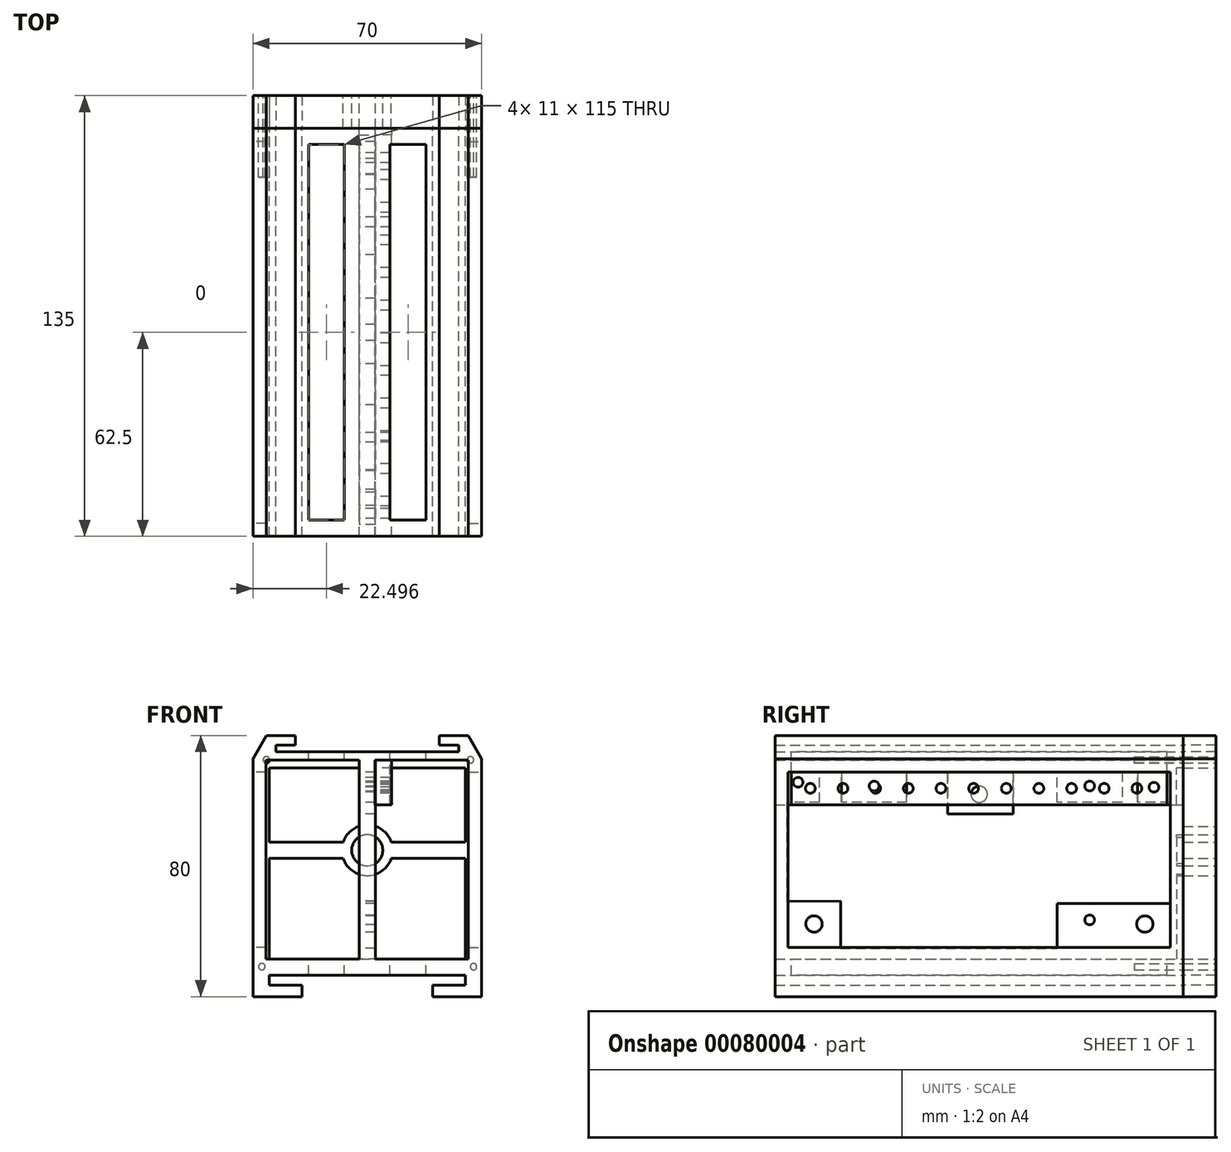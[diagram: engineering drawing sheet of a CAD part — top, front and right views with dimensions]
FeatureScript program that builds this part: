
annotation { "Feature Type Name" : "Feature", "Feature Type Description" : "" }
export const myFeature = defineFeature(function(context is Context, id is Id, definition is map)
    precondition{}
    {
        {
            var Q0;
            Q0=qCreatedBy(makeId("Front.planeOp"),FACE);
            var sketch = newSketch(context, id + "F0", { "sketchPlane" : qUnion([Q0])});
            skLineSegment(sketch, "E0", {"start": v(-44.21, 35.4) * mm, "end": v(-53.11, 35.4) * mm});
            skLineSegment(sketch, "E1", {"start": v(-57.21, 25.4) * mm, "end": v(-57.21, -44.6) * mm});
            skLineSegment(sketch, "E2", {"start": v(-57.21, -44.6) * mm, "end": v(-42.21, -44.6) * mm});
            skLineSegment(sketch, "E3", {"start": v(-42.21, -44.6) * mm, "end": v(-42.21, -41.16) * mm});
            skLineSegment(sketch, "E4", {"start": v(-42.21, -41.16) * mm, "end": v(-52.21, -41.16) * mm});
            skLineSegment(sketch, "E5", {"start": v(-52.21, -41.16) * mm, "end": v(-52.21, -38.06) * mm});
            skLineSegment(sketch, "E6", {"start": v(-52.21, -38.06) * mm, "end": v(-22.21, -38.06) * mm});
            skLineSegment(sketch, "E7", {"start": v(-44.21, 35.4) * mm, "end": v(-44.21, 32.4) * mm});
            skLineSegment(sketch, "E8", {"start": v(-44.21, 32.4) * mm, "end": v(-50.21, 32.4) * mm});
            skLineSegment(sketch, "E9", {"start": v(-50.21, 32.4) * mm, "end": v(-50.21, 30.4) * mm});
            skLineSegment(sketch, "E10", {"start": v(-50.21, 30.4) * mm, "end": v(-22.21, 30.4) * mm});
            skLineSegment(sketch, "E11", {"start": v(-22.21, 30.4) * mm, "end": v(-22.21, -38.06) * mm, "construction": true});
            skLineSegment(sketch, "E12.MirrorCS", {"start": v(-0.21, 35.4) * mm, "end": v(-0.21, 32.4) * mm});
            skLineSegment(sketch, "E13.MirrorCS", {"start": v(7.79, -41.16) * mm, "end": v(7.79, -38.06) * mm});
            skLineSegment(sketch, "E14.MirrorCS", {"start": v(-0.21, 32.4) * mm, "end": v(5.79, 32.4) * mm});
            skLineSegment(sketch, "E15.MirrorCS", {"start": v(-2.21, -41.16) * mm, "end": v(7.79, -41.16) * mm});
            skLineSegment(sketch, "E16.MirrorCS", {"start": v(-2.21, -44.6) * mm, "end": v(-2.21, -41.16) * mm});
            skLineSegment(sketch, "E17.MirrorCS", {"start": v(5.79, 32.4) * mm, "end": v(5.79, 30.4) * mm});
            skLineSegment(sketch, "E18.MirrorCS", {"start": v(5.79, 30.4) * mm, "end": v(-22.21, 30.4) * mm});
            skLineSegment(sketch, "E19.MirrorCS", {"start": v(12.79, 25.4) * mm, "end": v(12.79, -44.6) * mm});
            skLineSegment(sketch, "E20.MirrorCS", {"start": v(12.79, -44.6) * mm, "end": v(-2.21, -44.6) * mm});
            skLineSegment(sketch, "E21.MirrorCS", {"start": v(7.79, -38.06) * mm, "end": v(-22.21, -38.06) * mm});
            skLineSegment(sketch, "E22", {"start": v(-57.21, 25.4) * mm, "end": v(-57.21, 28.2) * mm});
            skPoint(sketch, "E23.start.orphan", {"position": v(-70.21, 35.4) * mm});
            skPoint(sketch, "E24.start.orphan", {"position": v(-62.21, 19.4) * mm});
            skPoint(sketch, "E25.start.orphan", {"position": v(-59.21, 19.4) * mm});
            skPoint(sketch, "E26.start.orphan", {"position": v(-59.21, 25.4) * mm});
            skPoint(sketch, "E27.MirrorCS.start.orphan", {"position": v(14.79, 25.4) * mm});
            skPoint(sketch, "E28.MirrorCS.end.orphan", {"position": v(14.79, 19.4) * mm});
            skPoint(sketch, "E28.MirrorCS.start.orphan", {"position": v(17.79, 19.4) * mm});
            skPoint(sketch, "E29.MirrorCS.end.orphan", {"position": v(25.79, 35.4) * mm});
            skLineSegment(sketch, "E30.MirrorCS", {"start": v(-92.21, 30.4) * mm, "end": v(-92.21, -38.06) * mm, "construction": true});
            skLineSegment(sketch, "E31.MirrorCS", {"start": v(-0.21, 35.4) * mm, "end": v(8.68, 35.4) * mm});
            skLineSegment(sketch, "E32.MirrorCS", {"start": v(12.79, 25.4) * mm, "end": v(12.79, 28.2) * mm});
            skPoint(sketch, "E33.MirrorCS.end.orphan", {"position": v(-57.21, 35.4) * mm});
            skLineSegment(sketch, "E34", {"start": v(-53.11, 35.4) * mm, "end": v(-57.21, 28.2) * mm});
            skLineSegment(sketch, "E35.MirrorCS", {"start": v(-73.15, 59.43) * mm, "end": v(-132.06, 24.57) * mm, "construction": true});
            skLineSegment(sketch, "E36.MirrorCS", {"start": v(8.68, 35.4) * mm, "end": v(12.79, 28.2) * mm});
            skPoint(sketch, "E37.MirrorCS.end.orphan", {"position": v(-53.11, 35.4) * mm});
            skPoint(sketch, "E37.MirrorCS.start.orphan", {"position": v(-57.64, 43.05) * mm});
            skPoint(sketch, "E38.orphan", {"position": v(12.79, 35.4) * mm});
            skSolve(sketch);
        }
        {
            var Q0;
            Q0 = qSketchRegion(id + "F0", true);
            extrude(context, id + "F1", {"entities" : qUnion([Q0]), "depth" : 125 * mm});
        }
        {
            var Q0;
            Q0=makeQuery(id+"F1.opExtrude","CAP_FACE",FACE,{"disambiguationData":[OSD([sQuery(id+"F0.wireOp",EDGE,"E0"),sQuery(id+"F0.wireOp",EDGE,"E1"),sQuery(id+"F0.wireOp",EDGE,"E2"),sQuery(id+"F0.wireOp",EDGE,"E3"),sQuery(id+"F0.wireOp",EDGE,"E4"),sQuery(id+"F0.wireOp",EDGE,"E5"),sQuery(id+"F0.wireOp",EDGE,"E6"),sQuery(id+"F0.wireOp",EDGE,"E7"),sQuery(id+"F0.wireOp",EDGE,"E8"),sQuery(id+"F0.wireOp",EDGE,"E9"),sQuery(id+"F0.wireOp",EDGE,"E10"),sQuery(id+"F0.wireOp",EDGE,"E12.MirrorCS"),sQuery(id+"F0.wireOp",EDGE,"E13.MirrorCS"),sQuery(id+"F0.wireOp",EDGE,"E14.MirrorCS"),sQuery(id+"F0.wireOp",EDGE,"E15.MirrorCS"),sQuery(id+"F0.wireOp",EDGE,"E16.MirrorCS"),sQuery(id+"F0.wireOp",EDGE,"E17.MirrorCS"),sQuery(id+"F0.wireOp",EDGE,"E18.MirrorCS"),sQuery(id+"F0.wireOp",EDGE,"E19.MirrorCS"),sQuery(id+"F0.wireOp",EDGE,"E20.MirrorCS"),sQuery(id+"F0.wireOp",EDGE,"E21.MirrorCS"),sQuery(id+"F0.wireOp",EDGE,"E22"),sQuery(id+"F0.wireOp",EDGE,"E31.MirrorCS"),sQuery(id+"F0.wireOp",EDGE,"E32.MirrorCS"),sQuery(id+"F0.wireOp",EDGE,"E34"),sQuery(id+"F0.wireOp",EDGE,"E36.MirrorCS")])],"isStart":true});
            var sketch = newSketch(context, id + "F2", { "sketchPlane" : qUnion([Q0])});
            skLineSegment(sketch, "E39", {"start": v(-8.79, 27.9) * mm, "end": v(-8.79, -33.06) * mm});
            skLineSegment(sketch, "E40", {"start": v(-8.79, -33.06) * mm, "end": v(19.71, -33.06) * mm});
            skLineSegment(sketch, "E41", {"start": v(19.71, -33.06) * mm, "end": v(19.71, 27.9) * mm});
            skLineSegment(sketch, "E42", {"start": v(19.71, 27.9) * mm, "end": v(-8.79, 27.9) * mm});
            skPoint(sketch, "E43", {"position": v(22.21, 30.4) * mm});
            skPoint(sketch, "E44", {"position": v(22.21, -38.06) * mm});
            skLineSegment(sketch, "E45", {"start": v(22.21, 30.4) * mm, "end": v(22.21, -38.06) * mm, "construction": true});
            skLineSegment(sketch, "E46.MirrorCS", {"start": v(53.21, 27.9) * mm, "end": v(53.21, -33.06) * mm});
            skLineSegment(sketch, "E47.MirrorCS", {"start": v(24.71, 27.9) * mm, "end": v(53.21, 27.9) * mm});
            skLineSegment(sketch, "E48.MirrorCS", {"start": v(24.71, -33.06) * mm, "end": v(24.71, 27.9) * mm});
            skLineSegment(sketch, "E49.MirrorCS", {"start": v(53.21, -33.06) * mm, "end": v(24.71, -33.06) * mm});
            skSolve(sketch);
        }
        {
            var Q0;
            Q0 = qSketchRegion(id + "F2", true);
            extrude(context, id + "F3", {"entities" : qUnion([Q0]), "operationType" : NewBodyOperationType.REMOVE, "oppositeDirection" : true, "depth" : 152.27 * mm});
        }
        {
            var Q0;
            Q0=makeQuery(id+"F1.opExtrude","SWEPT_FACE",FACE,{"disambiguationData":[OSD([sQuery(id+"F0.wireOp",EDGE,"E1"),sQuery(id+"F0.wireOp",EDGE,"E22")])]});
            var sketch = newSketch(context, id + "F4", { "sketchPlane" : qUnion([Q0])});
            skLineSegment(sketch, "E50", {"start": v(4, 24.2) * mm, "end": v(4, -29.6) * mm});
            skLineSegment(sketch, "E51", {"start": v(4, -29.6) * mm, "end": v(121, -29.6) * mm});
            skLineSegment(sketch, "E52", {"start": v(121, -29.6) * mm, "end": v(121, 24.2) * mm});
            skLineSegment(sketch, "E53", {"start": v(121, 24.2) * mm, "end": v(4, 24.2) * mm});
            skSolve(sketch);
        }
        {
            var Q0;
            Q0 = qSketchRegion(id + "F4", true);
            extrude(context, id + "F5", {"entities" : qUnion([Q0]), "operationType" : NewBodyOperationType.REMOVE, "oppositeDirection" : true, "depth" : 25 * mm});
        }
        {
            var Q0;
            Q0=makeQuery(id+"F3.boolean.opBoolean","COPY",FACE,{"derivedFrom":makeQuery(id+"F3.opExtrude","SWEPT_FACE",FACE,{"disambiguationData":[OSD([sQuery(id+"F2.wireOp",EDGE,"E41")])]})});
            var Q1;
            Q1=makeQuery(id+"F3.boolean.opBoolean","COPY",FACE,{"derivedFrom":makeQuery(id+"F3.opExtrude","SWEPT_FACE",FACE,{"disambiguationData":[OSD([sQuery(id+"F2.wireOp",EDGE,"E48.MirrorCS")])]})});
            cPlane(context, id + "F6", {"entities" : qUnion([Q0, Q1]), "cplaneType" : CPlaneType.MID_PLANE, "offset" : 150 * mm, "width" : 150 * mm, "height" : 150 * mm});
        }
        {
            var Q0;
            Q0=makeQuery(id+"F5.boolean.opBoolean","COPY",FACE,{"derivedFrom":makeQuery(id+"F5.opExtrude","SWEPT_FACE",FACE,{"disambiguationData":[OSD([sQuery(id+"F4.wireOp",EDGE,"E50")])]})});
            var Q1;
            Q1=makeQuery(id+"F5.boolean.opBoolean","COPY",FACE,{"derivedFrom":makeQuery(id+"F5.opExtrude","SWEPT_FACE",FACE,{"disambiguationData":[OSD([sQuery(id+"F4.wireOp",EDGE,"E51")])]})});
            var Q2;
            Q2=makeQuery(id+"F5.boolean.opBoolean","COPY",FACE,{"derivedFrom":makeQuery(id+"F5.opExtrude","SWEPT_FACE",FACE,{"disambiguationData":[OSD([sQuery(id+"F4.wireOp",EDGE,"E52")])]})});
            var Q3;
            Q3=makeQuery(id+"F5.boolean.opBoolean","COPY",FACE,{"derivedFrom":makeQuery(id+"F5.opExtrude","SWEPT_FACE",FACE,{"disambiguationData":[OSD([sQuery(id+"F4.wireOp",EDGE,"E53")])]})});
            var Q4;
            Q4=qCreatedBy(id+"F6.planeOp",FACE);
            mirror(context, id + "F7", {"operationType" : NewBodyOperationType.REMOVE, "faces" : qUnion([Q0, Q1, Q2, Q3]), "mirrorPlane" : qUnion([Q4]), "patternType" : MirrorType.FACE});
        }
        {
            var Q0;
            Q0=makeQuery(id+"F3.boolean.opBoolean","COPY",FACE,{"derivedFrom":makeQuery(id+"F3.opExtrude","SWEPT_FACE",FACE,{"disambiguationData":[OSD([sQuery(id+"F2.wireOp",EDGE,"E48.MirrorCS")])]})});
            var sketch = newSketch(context, id + "F8", { "sketchPlane" : qUnion([Q0])});
            skCircle(sketch, "E54", {"center": v(28.68, 19.9) * mm, "radius": 1.5 * mm});
            skCircle(sketch, "E55", {"center": v(94.68, 19.9) * mm, "radius": 1.5 * mm});
            skCircle(sketch, "E56", {"center": v(28.68, -21.1) * mm, "radius": 1.5 * mm});
            skLineSegment(sketch, "E57", {"start": v(18.68, 24.2) * mm, "end": v(18.68, 14.9) * mm});
            skLineSegment(sketch, "E58", {"start": v(18.68, 14.9) * mm, "end": v(38.68, 14.9) * mm});
            skLineSegment(sketch, "E59", {"start": v(38.68, 14.9) * mm, "end": v(38.68, 24.16) * mm});
            skLineSegment(sketch, "E60", {"start": v(38.68, 24.16) * mm, "end": v(84.68, 24.16) * mm});
            skLineSegment(sketch, "E61", {"start": v(84.68, 24.16) * mm, "end": v(84.68, 14.9) * mm});
            skLineSegment(sketch, "E62", {"start": v(84.68, 14.9) * mm, "end": v(104.68, 14.9) * mm});
            skLineSegment(sketch, "E63", {"start": v(104.68, 14.9) * mm, "end": v(104.68, 24.2) * mm});
            skLineSegment(sketch, "E64", {"start": v(104.68, 24.2) * mm, "end": v(121.44, 24.2) * mm});
            skLineSegment(sketch, "E65", {"start": v(121.44, 24.2) * mm, "end": v(121.44, -29.8) * mm});
            skLineSegment(sketch, "E66", {"start": v(121.44, -29.8) * mm, "end": v(38.68, -29.8) * mm});
            skLineSegment(sketch, "E67", {"start": v(38.68, -29.8) * mm, "end": v(38.68, -16.1) * mm});
            skLineSegment(sketch, "E68", {"start": v(38.68, -16.1) * mm, "end": v(18.68, -16.1) * mm});
            skLineSegment(sketch, "E69", {"start": v(18.68, -16.1) * mm, "end": v(18.68, -29.6) * mm});
            skLineSegment(sketch, "E70", {"start": v(18.68, -29.6) * mm, "end": v(4, -29.6) * mm});
            skLineSegment(sketch, "E71", {"start": v(4, -29.6) * mm, "end": v(4, 24.2) * mm});
            skLineSegment(sketch, "E72", {"start": v(4, 24.2) * mm, "end": v(18.68, 24.2) * mm});
            skLineSegment(sketch, "E73", {"start": v(4, 14.9) * mm, "end": v(14, 14.9) * mm});
            skLineSegment(sketch, "E74", {"start": v(14, 14.9) * mm, "end": v(14, 24.2) * mm});
            skLineSegment(sketch, "E75", {"start": v(111.44, 14.9) * mm, "end": v(121.44, 14.9) * mm});
            skLineSegment(sketch, "E76", {"start": v(111.44, 14.9) * mm, "end": v(111.44, 24.2) * mm});
            skPoint(sketch, "E77", {"position": v(9, 14.9) * mm});
            skPoint(sketch, "E78", {"position": v(14, 19.54) * mm});
            skCircle(sketch, "E79", {"center": v(9, 19.54) * mm, "radius": 1.5 * mm});
            skPoint(sketch, "E80", {"position": v(111.44, 19.54) * mm});
            skPoint(sketch, "E81", {"position": v(116.44, 14.9) * mm});
            skCircle(sketch, "E82", {"center": v(117.98, 21.07) * mm, "radius": 1.5 * mm});
            skCircle(sketch, "E83", {"center": v(113.09, -22.34) * mm, "radius": 2.5 * mm});
            skCircle(sketch, "E84", {"center": v(11.76, -22.4) * mm, "radius": 2.5 * mm});
            skCircle(sketch, "E85", {"center": v(62.5, 17.4) * mm, "radius": 2.5 * mm});
            skPoint(sketch, "E85.centerSnap0", {"position": v(62.5, 27.9) * mm});
            skLineSegment(sketch, "E86", {"start": v(104.9, -29.8) * mm, "end": v(104.9, -15.36) * mm});
            skLineSegment(sketch, "E87", {"start": v(104.9, -15.36) * mm, "end": v(121.44, -15.4) * mm});
            skLineSegment(sketch, "E88", {"start": v(18.68, -16.1) * mm, "end": v(4, -16.1) * mm});
            skLineSegment(sketch, "E89", {"start": v(52.1, 24.16) * mm, "end": v(52.1, 11.4) * mm});
            skLineSegment(sketch, "E90", {"start": v(52.1, 11.4) * mm, "end": v(72.17, 11.4) * mm});
            skLineSegment(sketch, "E91", {"start": v(72.17, 11.4) * mm, "end": v(72.17, 24.16) * mm});
            skSolve(sketch);
        }
        {
            var Q0;
            {var subQ7=sQuery(id+"F8.wireOp",EDGE,"E57");Q0=makeQuery(id+"F8.imprint","IMPRINT",FACE,{"disambiguationData":[TD([[makeQuery(id+"F8.imprint","IMPRINT",EDGE,{"derivedFrom":subQ7}),-1.0]])]});}
            var Q1;
            Q1=makeQuery(id+"F8.imprint","IMPRINT",FACE,{"disambiguationData":[TD([[makeQuery(id+"F8.imprint","IMPRINT",EDGE,{"derivedFrom":sQuery(id+"F8.wireOp",EDGE,"E79")}),1.0]])]});
            var Q2;
            Q2=makeQuery(id+"F8.imprint","IMPRINT",FACE,{"disambiguationData":[TD([[makeQuery(id+"F8.imprint","IMPRINT",EDGE,{"derivedFrom":sQuery(id+"F8.wireOp",EDGE,"E54")}),1.0]])]});
            var Q3;
            Q3=makeQuery(id+"F8.imprint","IMPRINT",FACE,{"disambiguationData":[TD([[makeQuery(id+"F8.imprint","IMPRINT",EDGE,{"derivedFrom":sQuery(id+"F8.wireOp",EDGE,"E55")}),1.0]])]});
            var Q4;
            Q4=makeQuery(id+"F8.imprint","IMPRINT",FACE,{"disambiguationData":[TD([[makeQuery(id+"F8.imprint","IMPRINT",EDGE,{"derivedFrom":sQuery(id+"F8.wireOp",EDGE,"qEVCjfM7-5hEM-15X9-niTZ-lJ1H4B1JHHPk")}),1.0]])]});
            var Q5;
            Q5=makeQuery(id+"F8.imprint","IMPRINT",FACE,{"disambiguationData":[TD([[makeQuery(id+"F8.imprint","IMPRINT",EDGE,{"derivedFrom":sQuery(id+"F8.wireOp",EDGE,"E56")}),1.0]])]});
            var Q6;
            Q6=makeQuery(id+"F8.imprint","IMPRINT",FACE,{"disambiguationData":[TD([[makeQuery(id+"F8.imprint","IMPRINT",EDGE,{"derivedFrom":sQuery(id+"F8.wireOp",EDGE,"E82")}),1.0]])]});
            var Q7;
            Q7=makeQuery(id+"F8.imprint","IMPRINT",FACE,{"disambiguationData":[TD([[makeQuery(id+"F8.imprint","IMPRINT",EDGE,{"derivedFrom":sQuery(id+"F8.wireOp",EDGE,"E85")}),1.0]])]});
            var Q8;
            Q8=makeQuery(id+"F8.imprint","IMPRINT",FACE,{"disambiguationData":[TD([[makeQuery(id+"F8.imprint","IMPRINT",EDGE,{"derivedFrom":sQuery(id+"F8.wireOp",EDGE,"E84")}),1.0]])]});
            var Q9;
            Q9=makeQuery(id+"F8.imprint","IMPRINT",FACE,{"disambiguationData":[TD([[makeQuery(id+"F8.imprint","IMPRINT",EDGE,{"derivedFrom":sQuery(id+"F8.wireOp",EDGE,"E83")}),1.0]])]});
            extrude(context, id + "F9", {"entities" : qUnion([Q0, Q1, Q2, Q3, Q4, Q5, Q6, Q7, Q8, Q9]), "operationType" : NewBodyOperationType.REMOVE, "endBound" : BoundingType.UP_TO_NEXT, "oppositeDirection" : true, "depth" : 2.5 * mm});
        }
        {
            var Q0;
            Q0=makeQuery(id+"F3.boolean.opBoolean","COPY",FACE,{"derivedFrom":makeQuery(id+"F3.opExtrude","SWEPT_FACE",FACE,{"disambiguationData":[OSD([sQuery(id+"F2.wireOp",EDGE,"E41")])]})});
            var sketch = newSketch(context, id + "F10", { "sketchPlane" : qUnion([Q0])});
            skLineSegment(sketch, "E92", {"start": v(-121.85, 14.2) * mm, "end": v(-4, 14.2) * mm});
            skCircle(sketch, "E93", {"center": v(-114.21, 19.2) * mm, "radius": 1.5 * mm});
            skCircle(sketch, "E94.1.0.0", {"center": v(-104.21, 19.2) * mm, "radius": 1.5 * mm});
            skCircle(sketch, "E94.2.0.0", {"center": v(-94.21, 19.2) * mm, "radius": 1.5 * mm});
            skCircle(sketch, "E94.3.0.0", {"center": v(-84.21, 19.2) * mm, "radius": 1.5 * mm});
            skCircle(sketch, "E94.4.0.0", {"center": v(-74.21, 19.2) * mm, "radius": 1.5 * mm});
            skCircle(sketch, "E94.5.0.0", {"center": v(-64.21, 19.2) * mm, "radius": 1.5 * mm});
            skCircle(sketch, "E94.6.0.0", {"center": v(-54.21, 19.2) * mm, "radius": 1.5 * mm});
            skCircle(sketch, "E94.7.0.0", {"center": v(-44.21, 19.2) * mm, "radius": 1.5 * mm});
            skCircle(sketch, "E94.8.0.0", {"center": v(-34.21, 19.2) * mm, "radius": 1.5 * mm});
            skCircle(sketch, "E94.9.0.0", {"center": v(-24.21, 19.2) * mm, "radius": 1.5 * mm});
            skCircle(sketch, "E94.10.0.0", {"center": v(-14.21, 19.2) * mm, "radius": 1.5 * mm});
            skLineSegment(sketch, "E94.direction1", {"start": v(-114.21, 19.2) * mm, "end": v(-104.21, 19.2) * mm, "construction": true});
            skLineSegment(sketch, "E95", {"start": v(-125, 27.9) * mm, "end": v(-125, 14.2) * mm});
            skLineSegment(sketch, "E96", {"start": v(-125, 14.2) * mm, "end": v(0, 14.2) * mm});
            skLineSegment(sketch, "E97", {"start": v(0, 14.2) * mm, "end": v(0, 27.9) * mm});
            skLineSegment(sketch, "E98", {"start": v(0, 27.9) * mm, "end": v(-125, 27.9) * mm});
            skLineSegment(sketch, "E99", {"start": v(-125, 14.2) * mm, "end": v(-125, 27.9) * mm});
            skSolve(sketch);
        }
        {
            var Q0;
            Q0=makeQuery(id+"F10.imprint","IMPRINT",FACE,{"disambiguationData":[TD([[makeQuery(id+"F10.imprint","IMPRINT",EDGE,{"derivedFrom":sQuery(id+"F10.wireOp",EDGE,"E94.4.0.0")}),-1.0]])]});
            var Q1;
            {var subQ0=sQuery(id+"F10.wireOp",EDGE,"E94.5.0.0");var subQ1=makeQuery(id+"F9.boolean.opBoolean","COPY",EDGE,{"derivedFrom":makeQuery(id+"F9.opExtrude","TWEAK_EDGE",EDGE,{"derivedFrom":[makeQuery(id+"F3.boolean.opBoolean","COPY",FACE,{"derivedFrom":makeQuery(id+"F3.opExtrude","SWEPT_FACE",FACE,{"disambiguationData":[OSD([sQuery(id+"F2.wireOp",EDGE,"E41")])]})}),makeQuery(id+"F8.imprint","IMPRINT",EDGE,{"derivedFrom":sQuery(id+"F8.wireOp",EDGE,"E85")})]})});var subQ2=makeQuery(id+"F10.imprint","INTERSECT",VERTEX,{"disambiguationData":[OD(0.0)],"derivedFrom":[subQ1,subQ0]});Q1=makeQuery(id+"F10.imprint","IMPRINT",FACE,{"disambiguationData":[TD([[makeQuery(id+"F10.imprint","IMPRINT",EDGE,{"disambiguationData":[TD([[subQ2,-1.0]])],"derivedFrom":subQ0}),-1.0]])]});}
            var Q2;
            Q2=makeQuery(id+"F10.imprint","IMPRINT",FACE,{"disambiguationData":[TD([[makeQuery(id+"F10.imprint","IMPRINT",EDGE,{"derivedFrom":sQuery(id+"F10.wireOp",EDGE,"E94.7.0.0")}),-1.0]])]});
            var Q3;
            Q3=makeQuery(id+"F10.imprint","IMPRINT",FACE,{"disambiguationData":[TD([[makeQuery(id+"F10.imprint","IMPRINT",EDGE,{"derivedFrom":sQuery(id+"F10.wireOp",EDGE,"E93")}),-1.0]])]});
            extrude(context, id + "F11", {"entities" : qUnion([Q0, Q1, Q2, Q3]), "depth" : 5 * mm, "hasSecondDirection" : true, "secondDirectionOppositeDirection" : true, "secondDirectionDepth" : .1 * mm});
        }
        {
            var Q0;
            Q0=makeQuery(id+"F1.opExtrude","CAP_FACE",FACE,{"disambiguationData":[OSD([sQuery(id+"F0.wireOp",EDGE,"E0"),sQuery(id+"F0.wireOp",EDGE,"E1"),sQuery(id+"F0.wireOp",EDGE,"E2"),sQuery(id+"F0.wireOp",EDGE,"E3"),sQuery(id+"F0.wireOp",EDGE,"E4"),sQuery(id+"F0.wireOp",EDGE,"E5"),sQuery(id+"F0.wireOp",EDGE,"E6"),sQuery(id+"F0.wireOp",EDGE,"E7"),sQuery(id+"F0.wireOp",EDGE,"E8"),sQuery(id+"F0.wireOp",EDGE,"E9"),sQuery(id+"F0.wireOp",EDGE,"E10"),sQuery(id+"F0.wireOp",EDGE,"E12.MirrorCS"),sQuery(id+"F0.wireOp",EDGE,"E13.MirrorCS"),sQuery(id+"F0.wireOp",EDGE,"E14.MirrorCS"),sQuery(id+"F0.wireOp",EDGE,"E15.MirrorCS"),sQuery(id+"F0.wireOp",EDGE,"E16.MirrorCS"),sQuery(id+"F0.wireOp",EDGE,"E17.MirrorCS"),sQuery(id+"F0.wireOp",EDGE,"E18.MirrorCS"),sQuery(id+"F0.wireOp",EDGE,"E19.MirrorCS"),sQuery(id+"F0.wireOp",EDGE,"E20.MirrorCS"),sQuery(id+"F0.wireOp",EDGE,"E21.MirrorCS"),sQuery(id+"F0.wireOp",EDGE,"E22"),sQuery(id+"F0.wireOp",EDGE,"E31.MirrorCS"),sQuery(id+"F0.wireOp",EDGE,"E32.MirrorCS"),sQuery(id+"F0.wireOp",EDGE,"E34"),sQuery(id+"F0.wireOp",EDGE,"E36.MirrorCS")])],"isStart":true});
            var sketch = newSketch(context, id + "F12", { "sketchPlane" : qUnion([Q0])});
            skLineSegment(sketch, "E100", {"start": v(0.21, 35.4) * mm, "end": v(-8.68, 35.4) * mm});
            skLineSegment(sketch, "E101", {"start": v(-8.68, 35.4) * mm, "end": v(-12.79, 28.2) * mm});
            skLineSegment(sketch, "E102", {"start": v(-12.79, 28.2) * mm, "end": v(-12.79, -44.6) * mm});
            skLineSegment(sketch, "E103", {"start": v(-12.79, -44.6) * mm, "end": v(2.21, -44.6) * mm});
            skLineSegment(sketch, "E104", {"start": v(2.21, -44.6) * mm, "end": v(2.21, -41.16) * mm});
            skLineSegment(sketch, "E105", {"start": v(2.21, -41.16) * mm, "end": v(-7.79, -41.16) * mm});
            skLineSegment(sketch, "E106", {"start": v(-7.79, -41.16) * mm, "end": v(-7.79, -38.06) * mm});
            skLineSegment(sketch, "E107", {"start": v(-7.79, -38.06) * mm, "end": v(52.21, -38.06) * mm});
            skLineSegment(sketch, "E108", {"start": v(52.21, -38.06) * mm, "end": v(52.21, -41.16) * mm});
            skLineSegment(sketch, "E109", {"start": v(52.21, -41.16) * mm, "end": v(42.21, -41.16) * mm});
            skLineSegment(sketch, "E110", {"start": v(42.21, -41.16) * mm, "end": v(42.21, -44.6) * mm});
            skLineSegment(sketch, "E111", {"start": v(42.21, -44.6) * mm, "end": v(57.21, -44.6) * mm});
            skLineSegment(sketch, "E112", {"start": v(57.21, -44.6) * mm, "end": v(57.21, 28.2) * mm});
            skLineSegment(sketch, "E113", {"start": v(57.21, 28.2) * mm, "end": v(53.11, 35.4) * mm});
            skLineSegment(sketch, "E114", {"start": v(53.11, 35.4) * mm, "end": v(44.21, 35.4) * mm});
            skLineSegment(sketch, "E115", {"start": v(44.21, 35.4) * mm, "end": v(44.21, 32.4) * mm});
            skLineSegment(sketch, "E116", {"start": v(44.21, 32.4) * mm, "end": v(50.21, 32.4) * mm});
            skLineSegment(sketch, "E117", {"start": v(50.21, 32.4) * mm, "end": v(50.21, 30.4) * mm});
            skLineSegment(sketch, "E118", {"start": v(50.21, 30.4) * mm, "end": v(-5.79, 30.4) * mm});
            skLineSegment(sketch, "E119", {"start": v(-5.79, 30.4) * mm, "end": v(-5.79, 32.4) * mm});
            skLineSegment(sketch, "E120", {"start": v(-5.79, 32.4) * mm, "end": v(0.21, 32.4) * mm});
            skLineSegment(sketch, "E121", {"start": v(0.21, 32.4) * mm, "end": v(0.21, 35.4) * mm});
            skSolve(sketch);
        }
        {
            var Q0;
            Q0 = qSketchRegion(id + "F12", true);
            extrude(context, id + "F13", {"entities" : qUnion([Q0]), "depth" : 10 * mm});
        }
        {
            var Q0;
            Q0=makeQuery(id+"F13.opExtrude","CAP_FACE",FACE,{"disambiguationData":[OSD([sQuery(id+"F12.wireOp",EDGE,"E100"),sQuery(id+"F12.wireOp",EDGE,"E101"),sQuery(id+"F12.wireOp",EDGE,"E102"),sQuery(id+"F12.wireOp",EDGE,"E103"),sQuery(id+"F12.wireOp",EDGE,"E104"),sQuery(id+"F12.wireOp",EDGE,"E105"),sQuery(id+"F12.wireOp",EDGE,"E106"),sQuery(id+"F12.wireOp",EDGE,"E107"),sQuery(id+"F12.wireOp",EDGE,"E108"),sQuery(id+"F12.wireOp",EDGE,"E109"),sQuery(id+"F12.wireOp",EDGE,"E110"),sQuery(id+"F12.wireOp",EDGE,"E111"),sQuery(id+"F12.wireOp",EDGE,"E112"),sQuery(id+"F12.wireOp",EDGE,"E113"),sQuery(id+"F12.wireOp",EDGE,"E114"),sQuery(id+"F12.wireOp",EDGE,"E115"),sQuery(id+"F12.wireOp",EDGE,"E116"),sQuery(id+"F12.wireOp",EDGE,"E117"),sQuery(id+"F12.wireOp",EDGE,"E118"),sQuery(id+"F12.wireOp",EDGE,"E119"),sQuery(id+"F12.wireOp",EDGE,"E120"),sQuery(id+"F12.wireOp",EDGE,"E121")])],"isStart":false});
            var sketch = newSketch(context, id + "F14", { "sketchPlane" : qUnion([Q0])});
            skPoint(sketch, "E122", {"position": v(22.21, 30.4) * mm});
            skLineSegment(sketch, "E123", {"start": v(22.21, 30.4) * mm, "end": v(22.21, -38.06) * mm, "construction": true});
            skCircle(sketch, "E124", {"center": v(22.21, 0.23) * mm, "radius": 4.76 * mm});
            skCircle(sketch, "E125", {"center": v(22.21, 0.23) * mm, "radius": 7.76 * mm});
            skLineSegment(sketch, "E126", {"start": v(19.71, 30.4) * mm, "end": v(19.71, 7.58) * mm});
            skLineSegment(sketch, "E127", {"start": v(14.86, -2.27) * mm, "end": v(-12.79, -2.27) * mm});
            skLineSegment(sketch, "E128", {"start": v(14.86, 2.73) * mm, "end": v(-12.79, 2.73) * mm});
            skLineSegment(sketch, "E129.MirrorCS", {"start": v(24.71, 30.4) * mm, "end": v(24.71, 7.58) * mm});
            skLineSegment(sketch, "E130.MirrorCS", {"start": v(29.56, 2.73) * mm, "end": v(57.21, 2.73) * mm});
            skLineSegment(sketch, "E131.MirrorCS", {"start": v(29.56, -2.27) * mm, "end": v(57.21, -2.27) * mm});
            skLineSegment(sketch, "E132", {"start": v(-12.79, 2.73) * mm, "end": v(-12.79, 28.2) * mm});
            skLineSegment(sketch, "E133", {"start": v(-12.79, 28.2) * mm, "end": v(-8.68, 35.4) * mm});
            skLineSegment(sketch, "E134", {"start": v(-8.68, 35.4) * mm, "end": v(0.21, 35.4) * mm});
            skLineSegment(sketch, "E135", {"start": v(0.21, 35.4) * mm, "end": v(0.21, 32.4) * mm});
            skLineSegment(sketch, "E136", {"start": v(0.21, 32.4) * mm, "end": v(-5.79, 32.4) * mm});
            skLineSegment(sketch, "E137", {"start": v(-5.79, 32.4) * mm, "end": v(-5.79, 30.4) * mm});
            skLineSegment(sketch, "E138", {"start": v(-5.79, 30.4) * mm, "end": v(19.71, 30.4) * mm});
            skLineSegment(sketch, "E139", {"start": v(-12.79, -2.27) * mm, "end": v(-12.79, -44.6) * mm});
            skLineSegment(sketch, "E140", {"start": v(-12.79, -44.6) * mm, "end": v(2.21, -44.6) * mm});
            skLineSegment(sketch, "E141", {"start": v(2.21, -44.6) * mm, "end": v(2.21, -41.16) * mm});
            skLineSegment(sketch, "E142", {"start": v(2.21, -41.16) * mm, "end": v(-7.79, -41.16) * mm});
            skLineSegment(sketch, "E143", {"start": v(-7.79, -41.16) * mm, "end": v(-7.79, -38.06) * mm});
            skLineSegment(sketch, "E144", {"start": v(-7.79, -38.06) * mm, "end": v(22.21, -38.06) * mm});
            skLineSegment(sketch, "E145.MirrorCS", {"start": v(52.21, -41.16) * mm, "end": v(52.21, -38.06) * mm});
            skLineSegment(sketch, "E146.MirrorCS", {"start": v(42.21, -44.6) * mm, "end": v(42.21, -41.16) * mm});
            skLineSegment(sketch, "E147.MirrorCS", {"start": v(57.21, -44.6) * mm, "end": v(42.21, -44.6) * mm});
            skLineSegment(sketch, "E148.MirrorCS", {"start": v(42.21, -41.16) * mm, "end": v(52.21, -41.16) * mm});
            skLineSegment(sketch, "E149.MirrorCS", {"start": v(57.21, -2.27) * mm, "end": v(57.21, -44.6) * mm});
            skLineSegment(sketch, "E150.MirrorCS", {"start": v(50.21, 32.4) * mm, "end": v(50.21, 30.4) * mm});
            skLineSegment(sketch, "E151.MirrorCS", {"start": v(44.21, 35.4) * mm, "end": v(44.21, 32.4) * mm});
            skLineSegment(sketch, "E152.MirrorCS", {"start": v(44.21, 32.4) * mm, "end": v(50.21, 32.4) * mm});
            skLineSegment(sketch, "E153.MirrorCS", {"start": v(57.21, 28.2) * mm, "end": v(53.11, 35.4) * mm});
            skLineSegment(sketch, "E154.MirrorCS", {"start": v(53.11, 35.4) * mm, "end": v(44.21, 35.4) * mm});
            skLineSegment(sketch, "E155.MirrorCS", {"start": v(50.21, 30.4) * mm, "end": v(24.71, 30.4) * mm});
            skLineSegment(sketch, "E156.MirrorCS", {"start": v(57.21, 2.73) * mm, "end": v(57.21, 28.2) * mm});
            skLineSegment(sketch, "E157.MirrorCS", {"start": v(52.21, -38.06) * mm, "end": v(22.21, -38.06) * mm});
            skLineSegment(sketch, "E158", {"start": v(19.71, 25.4) * mm, "end": v(-7.79, 25.4) * mm});
            skLineSegment(sketch, "E159", {"start": v(-7.79, 25.4) * mm, "end": v(-7.79, 2.73) * mm});
            skLineSegment(sketch, "E160", {"start": v(24.71, 25.4) * mm, "end": v(52.21, 25.4) * mm});
            skLineSegment(sketch, "E161", {"start": v(52.21, 25.4) * mm, "end": v(52.21, 2.73) * mm});
            skLineSegment(sketch, "E162", {"start": v(52.21, -2.25) * mm, "end": v(52.21, -33.06) * mm});
            skLineSegment(sketch, "E163", {"start": v(52.21, -33.06) * mm, "end": v(-7.79, -33.06) * mm});
            skLineSegment(sketch, "E164", {"start": v(-7.79, -33.06) * mm, "end": v(-7.79, -2.27) * mm});
            skSolve(sketch);
        }
        {
            var Q0;
            Q0=makeQuery(id+"F14.imprint","IMPRINT",FACE,{"disambiguationData":[TD([[makeQuery(id+"F14.imprint","IMPRINT",EDGE,{"derivedFrom":sQuery(id+"F14.wireOp",EDGE,"E124")}),1.0]])]});
            var Q1;
            {var subQ3=sQuery(id+"F14.wireOp",EDGE,"E158");Q1=makeQuery(id+"F14.imprint","IMPRINT",FACE,{"disambiguationData":[TD([[makeQuery(id+"F14.imprint","IMPRINT",EDGE,{"derivedFrom":subQ3}),1.0]])]});}
            var Q2;
            {var subQ0=sQuery(id+"F14.wireOp",EDGE,"E160");Q2=makeQuery(id+"F14.imprint","IMPRINT",FACE,{"disambiguationData":[TD([[makeQuery(id+"F14.imprint","IMPRINT",EDGE,{"derivedFrom":subQ0}),-1.0]])]});}
            var Q3;
            {var subQ0=sQuery(id+"F14.wireOp",EDGE,"E163");Q3=makeQuery(id+"F14.imprint","IMPRINT",FACE,{"disambiguationData":[TD([[makeQuery(id+"F14.imprint","IMPRINT",EDGE,{"derivedFrom":subQ0}),-1.0]])]});}
            extrude(context, id + "F15", {"entities" : qUnion([Q0, Q1, Q2, Q3]), "operationType" : NewBodyOperationType.REMOVE, "oppositeDirection" : true, "depth" : 12 * mm});
        }
        {
            var Q0;
            Q0=makeQuery(id+"F13.opExtrude","CAP_FACE",FACE,{"disambiguationData":[OSD([sQuery(id+"F12.wireOp",EDGE,"E100"),sQuery(id+"F12.wireOp",EDGE,"E101"),sQuery(id+"F12.wireOp",EDGE,"E102"),sQuery(id+"F12.wireOp",EDGE,"E103"),sQuery(id+"F12.wireOp",EDGE,"E104"),sQuery(id+"F12.wireOp",EDGE,"E105"),sQuery(id+"F12.wireOp",EDGE,"E106"),sQuery(id+"F12.wireOp",EDGE,"E107"),sQuery(id+"F12.wireOp",EDGE,"E108"),sQuery(id+"F12.wireOp",EDGE,"E109"),sQuery(id+"F12.wireOp",EDGE,"E110"),sQuery(id+"F12.wireOp",EDGE,"E111"),sQuery(id+"F12.wireOp",EDGE,"E112"),sQuery(id+"F12.wireOp",EDGE,"E113"),sQuery(id+"F12.wireOp",EDGE,"E114"),sQuery(id+"F12.wireOp",EDGE,"E115"),sQuery(id+"F12.wireOp",EDGE,"E116"),sQuery(id+"F12.wireOp",EDGE,"E117"),sQuery(id+"F12.wireOp",EDGE,"E118"),sQuery(id+"F12.wireOp",EDGE,"E119"),sQuery(id+"F12.wireOp",EDGE,"E120"),sQuery(id+"F12.wireOp",EDGE,"E121")])],"isStart":false});
            var sketch = newSketch(context, id + "F16", { "sketchPlane" : qUnion([Q0])});
            skCircle(sketch, "E165", {"center": v(-9.42, 27.92) * mm, "radius": 1 * mm});
            skCircle(sketch, "E166", {"center": v(-10.34, -35.44) * mm, "radius": 1 * mm});
            skCircle(sketch, "E167", {"center": v(54.5, -35.44) * mm, "radius": 1 * mm});
            skCircle(sketch, "E168", {"center": v(53.1, 27.92) * mm, "radius": 1 * mm});
            skSolve(sketch);
        }
        {
            var Q0;
            Q0 = qSketchRegion(id + "F16", true);
            extrude(context, id + "F17", {"entities" : qUnion([Q0]), "operationType" : NewBodyOperationType.REMOVE, "oppositeDirection" : true, "depth" : 25 * mm});
        }
        {
            var Q0;
            Q0=makeQuery(id+"F1.opExtrude","SWEPT_FACE",FACE,{"disambiguationData":[OSD([sQuery(id+"F0.wireOp",EDGE,"E10"),sQuery(id+"F0.wireOp",EDGE,"E18.MirrorCS")])]});
            var sketch = newSketch(context, id + "F18", { "sketchPlane" : qUnion([Q0])});
            skLineSegment(sketch, "E169", {"start": v(-22.21, 0) * mm, "end": v(-22.21, -125) * mm, "construction": true});
            skLineSegment(sketch, "E170.bottom", {"start": v(-40.21, -5) * mm, "end": v(-29.21, -5) * mm});
            skLineSegment(sketch, "E170.top", {"start": v(-40.21, -120) * mm, "end": v(-29.21, -120) * mm});
            skLineSegment(sketch, "E170.left", {"start": v(-40.21, -5) * mm, "end": v(-40.21, -120) * mm});
            skLineSegment(sketch, "E170.right", {"start": v(-29.21, -5) * mm, "end": v(-29.21, -120) * mm});
            skLineSegment(sketch, "E171.MirrorCS", {"start": v(-4.21, -5) * mm, "end": v(-15.21, -5) * mm});
            skLineSegment(sketch, "E172.MirrorCS", {"start": v(-4.21, -120) * mm, "end": v(-15.21, -120) * mm});
            skLineSegment(sketch, "E173.MirrorCS", {"start": v(-4.21, -5) * mm, "end": v(-4.21, -120) * mm});
            skLineSegment(sketch, "E174.MirrorCS", {"start": v(-15.21, -5) * mm, "end": v(-15.21, -120) * mm});
            skSolve(sketch);
        }
        {
            var Q0;
            Q0 = qSketchRegion(id + "F18", true);
            extrude(context, id + "F19", {"entities" : qUnion([Q0]), "operationType" : NewBodyOperationType.REMOVE, "oppositeDirection" : true, "depth" : 106.67 * mm});
        }
    });
